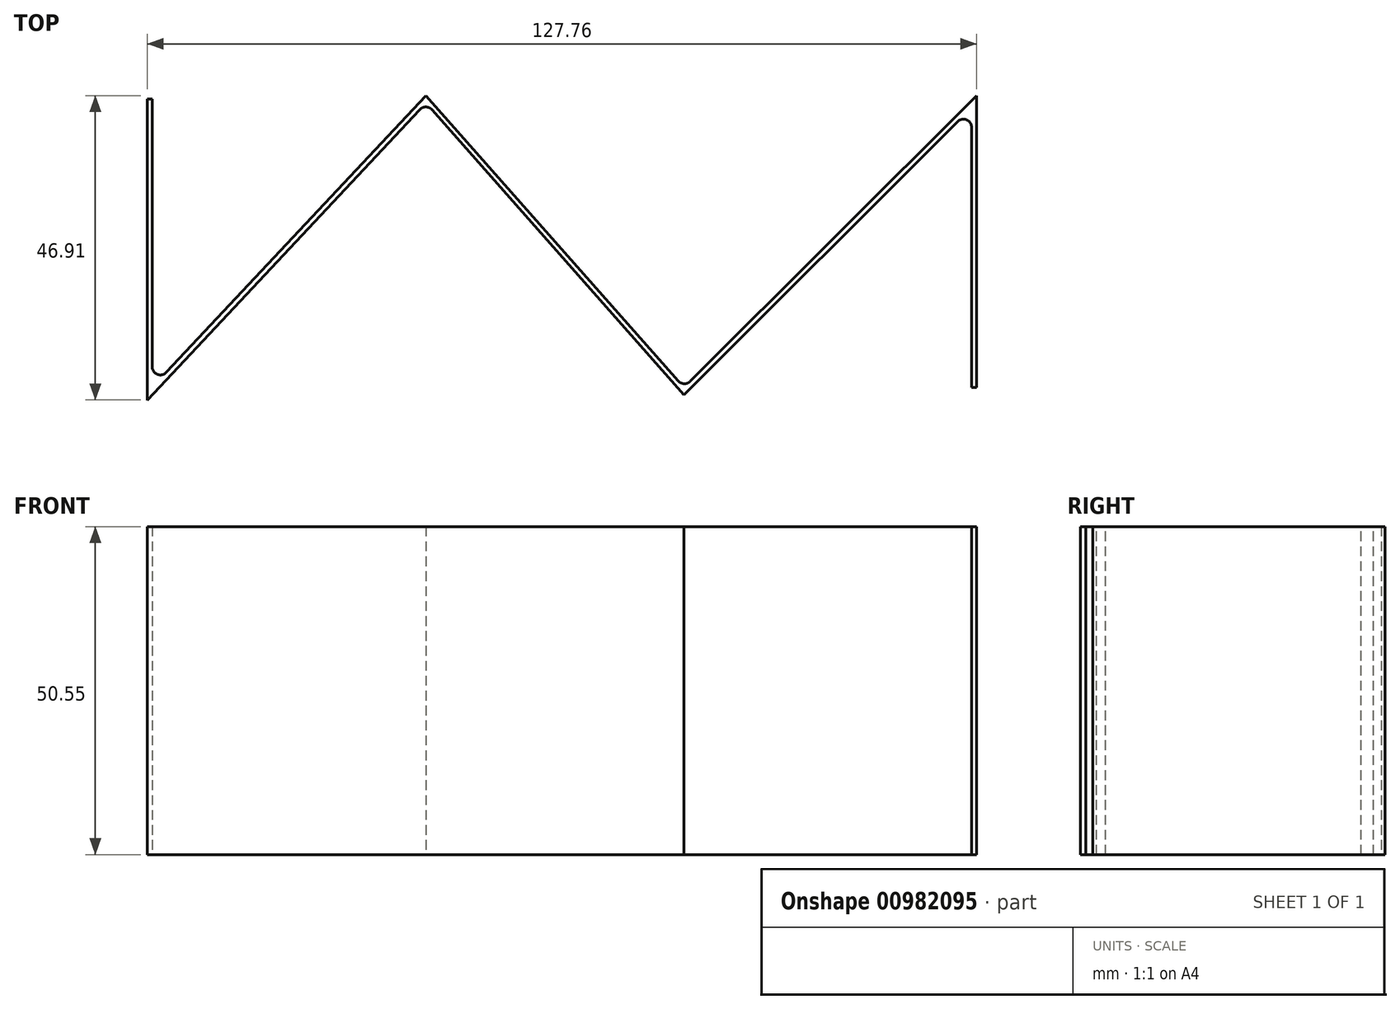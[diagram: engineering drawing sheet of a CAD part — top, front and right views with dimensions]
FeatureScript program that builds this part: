
annotation { "Feature Type Name" : "Feature", "Feature Type Description" : "" }
export const myFeature = defineFeature(function(context is Context, id is Id, definition is map)
    precondition{}
    {
        {
            var Q0;
            Q0=qCreatedBy(makeId("Top.planeOp"),FACE);
            var sketch = newSketch(context, id + "F0", { "sketchPlane" : qUnion([Q0])});
            skLineSegment(sketch, "E0", {"start": v(-31.62, 12.3) * mm, "end": v(-31.62, -32.15) * mm});
            skLineSegment(sketch, "E1", {"start": v(-31.62, -32.15) * mm, "end": v(10.57, 12.84) * mm});
            skLineSegment(sketch, "E2", {"start": v(10.57, 12.84) * mm, "end": v(50.32, -32.15) * mm});
            skLineSegment(sketch, "E3", {"start": v(50.32, -32.15) * mm, "end": v(95.38, 12.84) * mm});
            skLineSegment(sketch, "E4", {"start": v(95.38, 12.84) * mm, "end": v(95.38, -32.15) * mm});
            skLineSegment(sketch, "E5.0", {"start": v(94.62, 11) * mm, "end": v(94.62, -32.15) * mm});
            skLineSegment(sketch, "E5.1", {"start": v(-32.38, 12.3) * mm, "end": v(-32.38, -34.07) * mm});
            skLineSegment(sketch, "E5.2", {"start": v(-32.38, -34.07) * mm, "end": v(10.56, 11.7) * mm});
            skLineSegment(sketch, "E5.3", {"start": v(10.56, 11.7) * mm, "end": v(50.29, -33.26) * mm});
            skLineSegment(sketch, "E5.4", {"start": v(50.29, -33.26) * mm, "end": v(94.62, 11) * mm});
            skLineSegment(sketch, "E6", {"start": v(-32.38, 12.3) * mm, "end": v(-31.62, 12.3) * mm});
            skLineSegment(sketch, "E7", {"start": v(94.62, -32.15) * mm, "end": v(95.38, -32.15) * mm});
            skSolve(sketch);
        }
        {
            var Q0;
            Q0 = qSketchRegion(id + "F0", true);
            extrude(context, id + "F1", {"entities" : qUnion([Q0]), "depth" : 50.55 * mm, "offsetDistance" : 25.4 * mm});
        }
        {
            var Q0;
            Q0=makeQuery(id+"F1.opExtrude","SWEPT_EDGE",EDGE,{"disambiguationData":[OSD([sQuery(id+"F0.wireOp",EDGE,"E5.2"),sQuery(id+"F0.wireOp",EDGE,"E5.3")])]});
            var Q1;
            Q1=makeQuery(id+"F1.opExtrude","SWEPT_EDGE",EDGE,{"disambiguationData":[OSD([sQuery(id+"F0.wireOp",EDGE,"E0"),sQuery(id+"F0.wireOp",EDGE,"E1")])]});
            var Q2;
            Q2=makeQuery(id+"F1.opExtrude","SWEPT_EDGE",EDGE,{"disambiguationData":[OSD([sQuery(id+"F0.wireOp",EDGE,"E2"),sQuery(id+"F0.wireOp",EDGE,"E3")])]});
            var Q3;
            Q3=makeQuery(id+"F1.opExtrude","SWEPT_EDGE",EDGE,{"disambiguationData":[OSD([sQuery(id+"F0.wireOp",EDGE,"E5.0"),sQuery(id+"F0.wireOp",EDGE,"E5.4")])]});
            fillet(context, id + "F2", {"entities" : qUnion([Q0, Q1, Q2, Q3]), "radius" : 1.27 * mm, "tangentPropagation" : true, "allowEdgeOverflow" : false});
        }
    });
